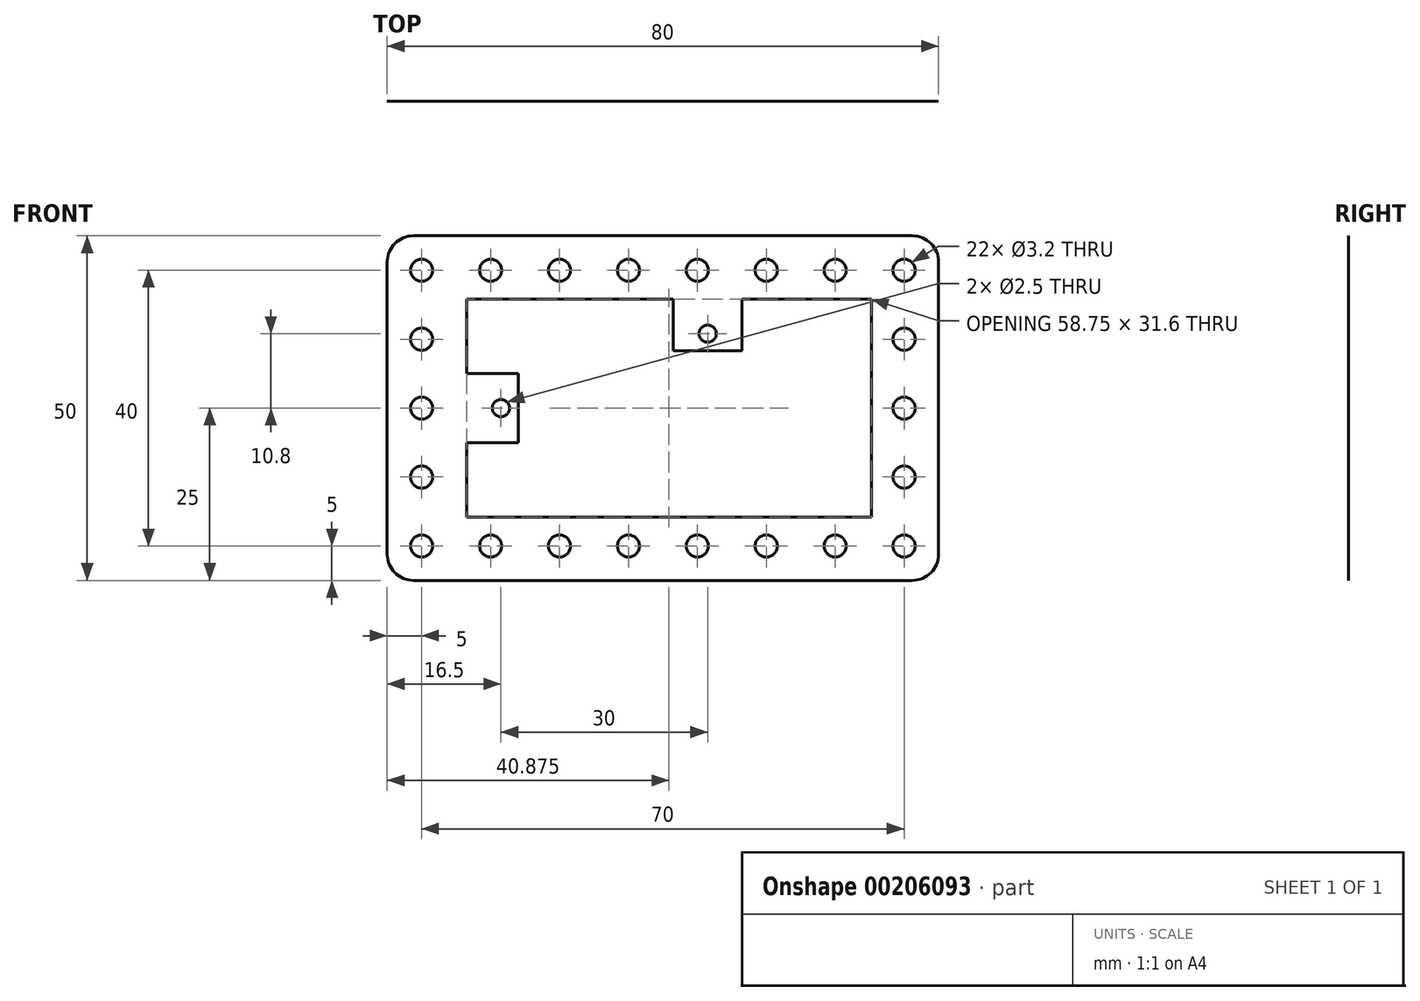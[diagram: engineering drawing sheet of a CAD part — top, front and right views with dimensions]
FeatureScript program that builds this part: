
annotation { "Feature Type Name" : "Feature", "Feature Type Description" : "" }
export const myFeature = defineFeature(function(context is Context, id is Id, definition is map)
    precondition{}
    {
        {
            var Q0;
            Q0=qCreatedBy(makeId("Front.planeOp"),FACE);
            var sketch = newSketch(context, id + "F0", { "sketchPlane" : qUnion([Q0])});
            skCircle(sketch, "E0", {"center": v(31.75, -1.75) * mm, "radius": 1.25 * mm});
            skCircle(sketch, "E1", {"center": v(1.75, -12.55) * mm, "radius": 1.25 * mm});
            skLineSegment(sketch, "E2.bottom", {"start": v(36.75, -4.25) * mm, "end": v(26.75, -4.25) * mm});
            skLineSegment(sketch, "E2.left", {"start": v(36.75, -4.25) * mm, "end": v(36.75, 3.25) * mm});
            skLineSegment(sketch, "E2.right", {"start": v(26.75, -4.25) * mm, "end": v(26.75, 3.25) * mm});
            skLineSegment(sketch, "E3.bottom", {"start": v(-3.25, -7.55) * mm, "end": v(4.25, -7.55) * mm});
            skLineSegment(sketch, "E3.top", {"start": v(-3.25, -17.55) * mm, "end": v(4.25, -17.55) * mm});
            skLineSegment(sketch, "E3.right", {"start": v(4.25, -7.55) * mm, "end": v(4.25, -17.55) * mm});
            skLineSegment(sketch, "E4.bottom", {"start": v(-10.94, 12.45) * mm, "end": v(61.44, 12.45) * mm});
            skLineSegment(sketch, "E4.top", {"start": v(-10.94, -37.55) * mm, "end": v(61.44, -37.55) * mm});
            skLineSegment(sketch, "E4.left", {"start": v(-14.75, 8.64) * mm, "end": v(-14.75, -33.74) * mm});
            skLineSegment(sketch, "E4.right", {"start": v(65.25, 8.64) * mm, "end": v(65.25, -33.74) * mm});
            skLineSegment(sketch, "E5.bottom", {"start": v(-3.25, 3.25) * mm, "end": v(26.75, 3.25) * mm});
            skLineSegment(sketch, "E5.left", {"start": v(-3.25, 3.25) * mm, "end": v(-3.25, -7.55) * mm});
            skLineSegment(sketch, "E5.right", {"start": v(55.5, 3.25) * mm, "end": v(55.5, -28.35) * mm});
            skPoint(sketch, "E6.orphan", {"position": v(0, 0) * mm});
            skLineSegment(sketch, "E7.trimOffspring", {"start": v(36.75, 3.25) * mm, "end": v(55.5, 3.25) * mm});
            skLineSegment(sketch, "E8.trimOffspring", {"start": v(-3.25, -17.55) * mm, "end": v(-3.25, -28.35) * mm});
            skCircle(sketch, "E9", {"center": v(-9.75, 7.45) * mm, "radius": 1.6 * mm});
            skCircle(sketch, "E10.1.0.0", {"center": v(0.25, 7.45) * mm, "radius": 1.6 * mm});
            skCircle(sketch, "E10.2.0.0", {"center": v(10.25, 7.45) * mm, "radius": 1.6 * mm});
            skCircle(sketch, "E10.3.0.0", {"center": v(20.25, 7.45) * mm, "radius": 1.6 * mm});
            skCircle(sketch, "E10.4.0.0", {"center": v(30.25, 7.45) * mm, "radius": 1.6 * mm});
            skCircle(sketch, "E10.5.0.0", {"center": v(40.25, 7.45) * mm, "radius": 1.6 * mm});
            skCircle(sketch, "E10.6.0.0", {"center": v(50.25, 7.45) * mm, "radius": 1.6 * mm});
            skCircle(sketch, "E10.7.0.0", {"center": v(60.25, 7.45) * mm, "radius": 1.6 * mm});
            skLineSegment(sketch, "E10.direction1", {"start": v(-9.75, 7.45) * mm, "end": v(0.25, 7.45) * mm, "construction": true});
            skCircle(sketch, "E11.0.1.0", {"center": v(-9.75, -2.55) * mm, "radius": 1.6 * mm});
            skCircle(sketch, "E11.0.2.0", {"center": v(-9.75, -12.55) * mm, "radius": 1.6 * mm});
            skCircle(sketch, "E11.0.3.0", {"center": v(-9.75, -22.55) * mm, "radius": 1.6 * mm});
            skCircle(sketch, "E11.0.4.0", {"center": v(-9.75, -32.55) * mm, "radius": 1.6 * mm});
            skLineSegment(sketch, "E11.direction1", {"start": v(-9.75, 7.45) * mm, "end": v(15.65, 7.45) * mm, "construction": true});
            skLineSegment(sketch, "E11.direction2", {"start": v(-9.75, 7.45) * mm, "end": v(-9.75, -2.55) * mm, "construction": true});
            skCircle(sketch, "E12.1.0.0", {"center": v(0.25, -32.55) * mm, "radius": 1.6 * mm});
            skCircle(sketch, "E12.2.0.0", {"center": v(10.25, -32.55) * mm, "radius": 1.6 * mm});
            skCircle(sketch, "E12.3.0.0", {"center": v(20.25, -32.55) * mm, "radius": 1.6 * mm});
            skCircle(sketch, "E12.4.0.0", {"center": v(30.25, -32.55) * mm, "radius": 1.6 * mm});
            skCircle(sketch, "E12.5.0.0", {"center": v(40.25, -32.55) * mm, "radius": 1.6 * mm});
            skCircle(sketch, "E12.6.0.0", {"center": v(50.25, -32.55) * mm, "radius": 1.6 * mm});
            skCircle(sketch, "E12.7.0.0", {"center": v(60.25, -32.55) * mm, "radius": 1.6 * mm});
            skLineSegment(sketch, "E12.direction1", {"start": v(-9.75, -32.55) * mm, "end": v(0.25, -32.55) * mm, "construction": true});
            skCircle(sketch, "E13.0.1.0", {"center": v(60.25, -2.55) * mm, "radius": 1.6 * mm});
            skCircle(sketch, "E13.0.2.0", {"center": v(60.25, -12.55) * mm, "radius": 1.6 * mm});
            skCircle(sketch, "E13.0.3.0", {"center": v(60.25, -22.55) * mm, "radius": 1.6 * mm});
            skLineSegment(sketch, "E13.direction1", {"start": v(60.25, 7.45) * mm, "end": v(85.65, 7.45) * mm, "construction": true});
            skLineSegment(sketch, "E13.direction2", {"start": v(60.25, 7.45) * mm, "end": v(60.25, -2.55) * mm, "construction": true});
            skPoint(sketch, "E14.visualSharp", {"position": v(-14.75, 12.45) * mm});
            skArc(sketch, "E14.filletArc", {"start": v(-10.94, 12.45) * mm, "mid": v(-13.63, 11.33) * mm, "end": v(-14.75, 8.64) * mm});
            skPoint(sketch, "E15.visualSharp", {"position": v(65.25, 12.45) * mm});
            skArc(sketch, "E15.filletArc", {"start": v(65.25, 8.64) * mm, "mid": v(64.13, 11.33) * mm, "end": v(61.44, 12.45) * mm});
            skPoint(sketch, "E16.visualSharp", {"position": v(65.25, -37.55) * mm});
            skArc(sketch, "E16.filletArc", {"start": v(61.44, -37.55) * mm, "mid": v(64.13, -36.43) * mm, "end": v(65.25, -33.74) * mm});
            skPoint(sketch, "E17.visualSharp", {"position": v(-14.75, -37.55) * mm});
            skArc(sketch, "E17.filletArc", {"start": v(-14.75, -33.74) * mm, "mid": v(-13.63, -36.43) * mm, "end": v(-10.94, -37.55) * mm});
            skLineSegment(sketch, "E18", {"start": v(-3.25, -28.35) * mm, "end": v(55.5, -28.35) * mm});
            skSolve(sketch);
        }
        {
            var Q0;
            Q0=makeQuery(id+"F0.imprint","IMPRINT",FACE,{"disambiguationData":[TD([[makeQuery(id+"F0.imprint","IMPRINT",EDGE,{"derivedFrom":sQuery(id+"F0.wireOp",EDGE,"E0")}),-1.0]])]});
            extrude(context, id + "F1", {"entities" : qUnion([Q0]), "depth" : 1 / 203.2 * mm});
        }
    });
